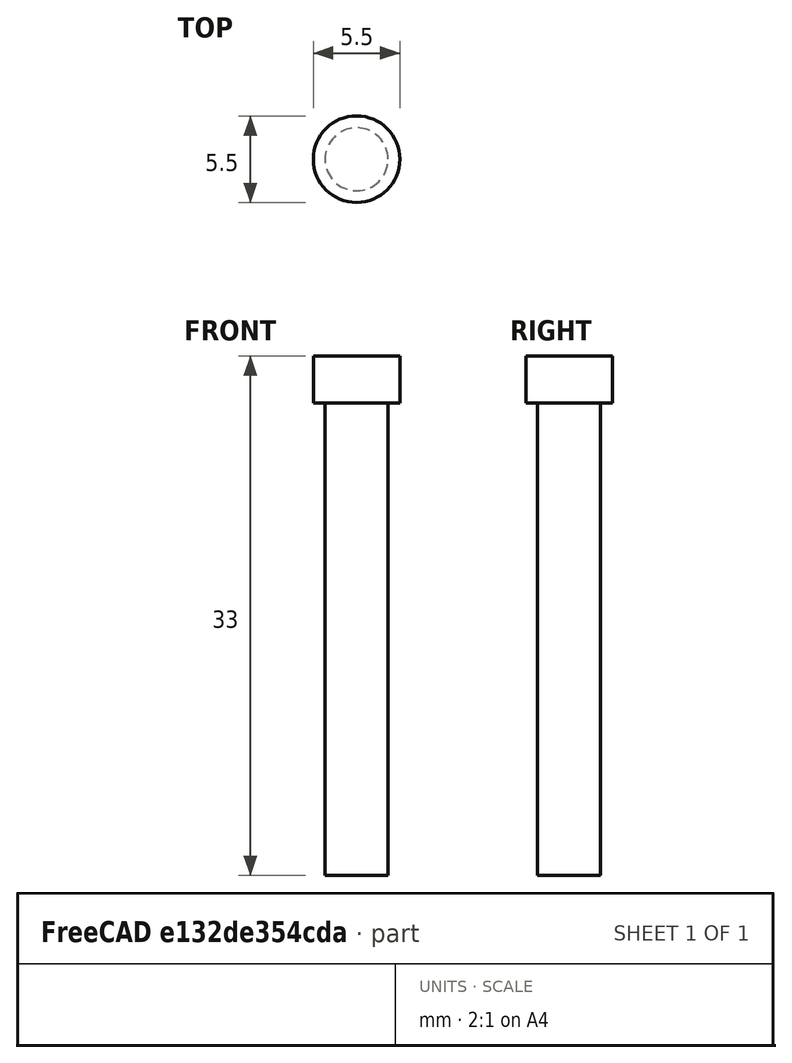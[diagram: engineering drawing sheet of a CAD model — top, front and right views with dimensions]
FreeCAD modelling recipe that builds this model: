
FCSTD DOCUMENT  (FreeCAD 0.18R14555 (Git shallow))
Label: m4-30
License: All rights reserved
LicenseURL: http://en.wikipedia.org/wiki/All_rights_reserved
objects: Sketcher::SketchObject×1, PartDesign::Revolution×1, PartDesign::Body×1
note: 4 computed .brp shape members not serialized (recipe doc carries the construction recipe); baked Part::Feature solids carry a one-line shape summary decoded from their .brp

FEATURE [Sketcher::SketchObject] Sketch
  MapMode = 5
  Placement = pos=(0,0,0) rot=(1,0,0;1.5708rad)
  Support = -> [XZ_Plane]
  sketch-geometry (6):
    g0: LineSegment StartX=0 StartY=0 StartZ=0 EndX=0 EndY=33 EndZ=0
    g1: LineSegment StartX=0 StartY=33 StartZ=0 EndX=2.75 EndY=33 EndZ=0
    g2: LineSegment StartX=2.75 StartY=33 StartZ=0 EndX=2.75 EndY=30 EndZ=0
    g3: LineSegment StartX=2.75 StartY=30 StartZ=0 EndX=2 EndY=30 EndZ=0
    g4: LineSegment StartX=2 StartY=30 StartZ=0 EndX=2 EndY=0 EndZ=0
    g5: LineSegment StartX=2 StartY=0 StartZ=0 EndX=0 EndY=0 EndZ=0
  constraints (17):
    c: Vertical(g0)
    c: Coincident(g0,g1)
    c: Horizontal(g1)
    c: Coincident(g1,g2)
    c: Vertical(g2)
    c: Coincident(g2,g3)
    c: Horizontal(g3)
    c: Coincident(g3,g4)
    c: Vertical(g4)
    c: Coincident(g4,g5)
    c: Coincident(g5,g0)
    c: Horizontal(g5)
    c: Coincident(g0,g-1)
    c: DistanceX(g5,g5) = 2
    c: DistanceY(g4,g4) = 30
    c: DistanceX(g1,g1) = 2.75
    c: DistanceY(g2,g2) = 3
FEATURE [PartDesign::Revolution] Revolution
  Angle = 360
  Axis = (0,2e-16,1)
  Base = (0,0,0)
  Placement = pos=(0,0,0) rot=(1,0,0;1.5708rad)
  Profile = -> Sketch
  ReferenceAxis = -> Sketch [V_Axis]
  Reversed = true
FEATURE [PartDesign::Body] Body
  Group = -> [Sketch,Revolution]
  Origin = -> Origin
  Tip = -> Revolution
